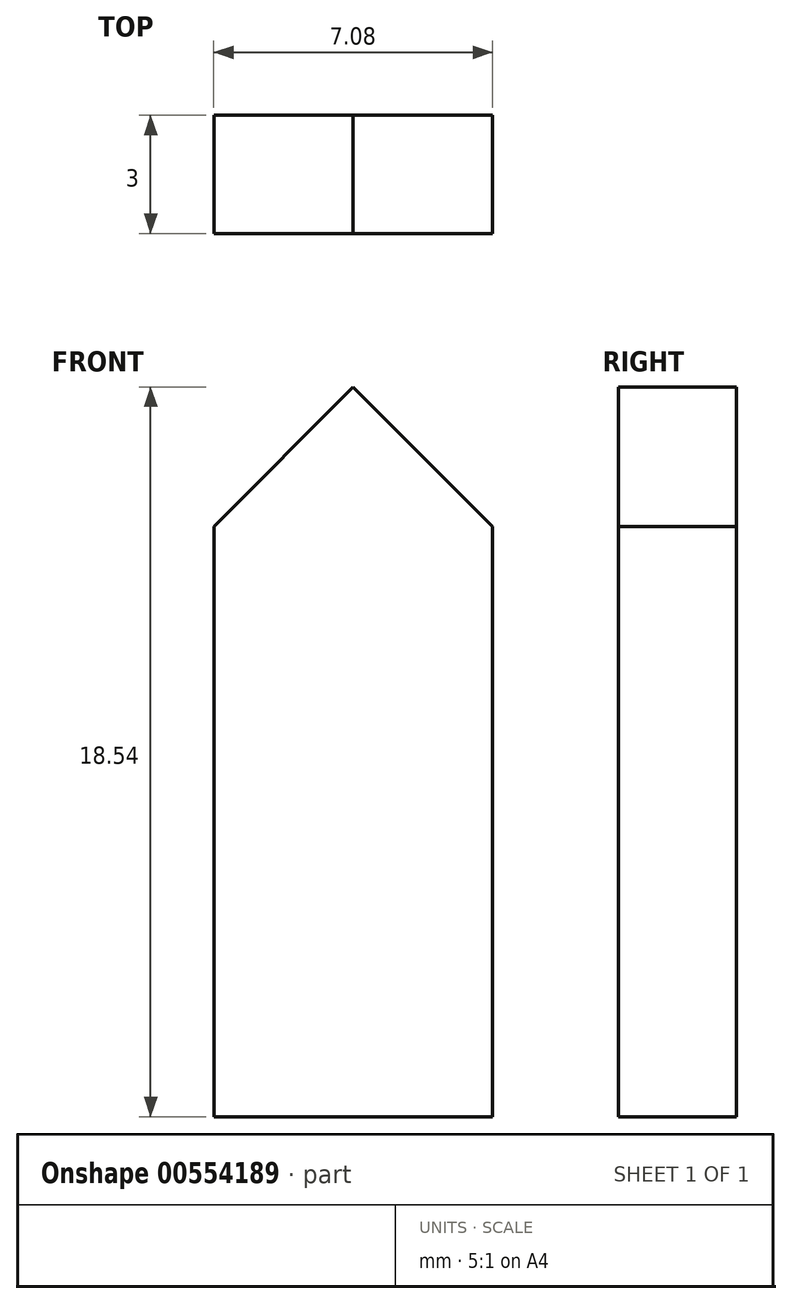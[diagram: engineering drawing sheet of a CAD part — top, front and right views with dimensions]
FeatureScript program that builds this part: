
annotation { "Feature Type Name" : "Feature", "Feature Type Description" : "" }
export const myFeature = defineFeature(function(context is Context, id is Id, definition is map)
    precondition{}
    {
        {
            var Q0;
            Q0=qCreatedBy(makeId("Front.planeOp"),FACE);
            var sketch = newSketch(context, id + "F0", { "sketchPlane" : qUnion([Q0])});
            skLineSegment(sketch, "E0", {"start": v(0, 0) * mm, "end": v(-3.54, 0) * mm});
            skLineSegment(sketch, "E1", {"start": v(-3.54, 0) * mm, "end": v(0, 3.54) * mm});
            skLineSegment(sketch, "E2", {"start": v(0, 3.54) * mm, "end": v(3.54, 0) * mm});
            skLineSegment(sketch, "E3", {"start": v(3.54, 0) * mm, "end": v(0, 0) * mm});
            skLineSegment(sketch, "E4", {"start": v(-3.54, 0) * mm, "end": v(-3.54, -15) * mm});
            skLineSegment(sketch, "E5", {"start": v(-3.54, -15) * mm, "end": v(3.54, -15) * mm});
            skLineSegment(sketch, "E6", {"start": v(3.54, -15) * mm, "end": v(3.54, 0) * mm});
            skSolve(sketch);
        }
        {
            var Q0;
            Q0=makeQuery(id+"F0.imprint","IMPRINT",FACE,{"disambiguationData":[TD([[makeQuery(id+"F0.imprint","IMPRINT",EDGE,{"derivedFrom":sQuery(id+"F0.wireOp",EDGE,"E0")}),1.0]])]});
            var Q1;
            Q1=makeQuery(id+"F0.imprint","IMPRINT",FACE,{"disambiguationData":[TD([[makeQuery(id+"F0.imprint","IMPRINT",EDGE,{"derivedFrom":sQuery(id+"F0.wireOp",EDGE,"E0")}),-1.0]])]});
            extrude(context, id + "F1", {"entities" : qUnion([Q0, Q1]), "depth" : 3 * mm, "offsetDistance" : 25 * mm});
        }
    });
